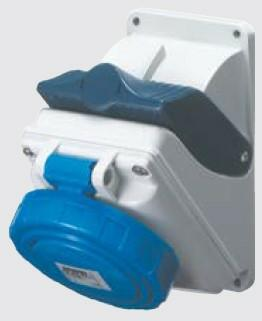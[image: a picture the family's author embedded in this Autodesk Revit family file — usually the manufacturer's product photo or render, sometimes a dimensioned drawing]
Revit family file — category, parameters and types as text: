
# Revit family: Building-ConnessioniIEC309-GEWISS-COMBIBLOC-PRESE-INTERBLOCCATE_IP55_SENZA_FONDO
name_source: partatom
category: Apparecchi elettrici
units: mm (PartAtom-declared; Revit-internal decimal feet)

## family parameters
Condiviso = No
Host = Superficie
Mantenere orientamento annotazione = Sì
Punto di calcolo locali = Sì
Quota connettore circolare = Usa diametro
Taglio con vuoti quando caricato = No
Tipo di parte = Normale

## types (18) — shared parameters
BLOCCO = B=C
Catalogo = BUILDING
Codice Electrocod = 2221
Con fondo = No
FORMULA = 1000 mm  [stored 3.28084 ft]
Frequenza = 50/60 Hz
Glow wire test: = 850 °C (Parti attive) - 650 °C (Parti passive)
Grado di protezione = IP55
IDF = d30aeb64-b42c-4c03-8e60-3032abfc95de
IDT = 73411960965b40fc900c2c175d51bdd6
Immagine tipo = COMBIBLOC55.jpg
L = 155 mm
N.poli = 1
POMELLO = bianco
PRESA = Giallo
Produttore = GEWISS S.p.A.
Prospetto di default = 1219 mm
Protezione = NO (SBF)
Resistenza agli urti = IK08
SEO = Presa interbloccata
STRUTTURA = RAL - 7035
STRUTTURA ALTA = blue
Scheda Tecnica = https://www.gewiss.com
Spostamento_S = 1500 mm
Temperatura di utilizzo = -25 +40 °C
Termopressione con biglia = 125 °C
Tipologia = Compatta
URL = https://www.gewiss.com
VETRO = Vetro
Versione file RFA = 21.4
Voltaggio = 0 V
W = 115 mm

## per-type parameters (varying)
| type | Colore: | Corrente nominale (A) | Descrizione | Modello | N. poli | Riferimento h | Tensione nominale |
| GW66474 - COMBIBLOC S.F.IP55 3P+T 16A 400V 6H | Rosso | 16 | COMBIBLOC S.F.IP55 3P+T 16A 400V 6H | GW66474 | 3P+T | 6 | 380-415V |
| GW66480 - COMBIBLOC S.F.IP55 3P+N+T 32A 110V 4H | Giallo | 32 | COMBIBLOC S.F.IP55 3P+N+T 32A 110V 4H | GW66480 | 3P+N+T | 4 | 100-130V |
| GW66479 - COMBIBLOC S.F.IP55 3P+T 32A 110V 4H | Giallo | 32 | COMBIBLOC S.F.IP55 3P+T 32A 110V 4H | GW66479 | 3P+T | 4 | 100-130V |
| GW66467 - COMBIBLOC S.F.IP55 2P+T 16A 110V 4H | Giallo | 16 | COMBIBLOC S.F.IP55 2P+T 16A 110V 4H | GW66467 | 2P+T | 4 | 100-130V |
| GW66469 - COMBIBLOC S.F.IP55 3P+N+T 16A 110V 4H | Giallo | 16 | COMBIBLOC S.F.IP55 3P+N+T 16A 110V 4H | GW66469 | 3P+N+T | 4 | 100-130V |
| GW66484 - COMBIBLOC S.F.IP55 2P+T 32A 400V 9H | Rosso | 32 | COMBIBLOC S.F.IP55 2P+T 32A 400V 9H | GW66484 | 2P+T | 9 | 380-415V |
| GW66478 - COMBIBLOC S.F.IP55 2P+T 32A 110V 4H | Giallo | 32 | COMBIBLOC S.F.IP55 2P+T 32A 110V 4H | GW66478 | 2P+T | 4 | 100-130V |
| GW66475 - COMBIBLOC S.F.IP55 3P+N+T 16A 400V 6H | Rosso | 16 | COMBIBLOC S.F.IP55 3P+N+T 16A 400V 6H | GW66475 | 3P+N+T | 6 | 380-415V |
| GW66486 - COMBIBLOC S.F.IP55 3P+N+T 32A 400V 6H | Rosso | 32 | COMBIBLOC S.F.IP55 3P+N+T 32A 400V 6H | GW66486 | 3P+N+T | 6 | 380-415V |
| GW66473 - COMBIBLOC S.F.IP55 2P+T 16A 400V 9H | Rosso | 16 | COMBIBLOC S.F.IP55 2P+T 16A 400V 9H | GW66473 | 2P+T | 9 | 380-415V |
| GW66482 - COMBIBLOC S.F.IP55 3P+T 32A 230V 9H | Blu | 32 | COMBIBLOC S.F.IP55 3P+T 32A 230V 9H | GW66482 | 3P+T | 9 | 200-250V |
| GW66483 - COMBIBLOC S.F.IP55 3P+N+T 32A 230V 9H | Blu | 32 | COMBIBLOC S.F.IP55 3P+N+T 32A 230V 9H | GW66483 | 3P+N+T | 9 | 200-250V |
| GW66472 - COMBIBLOC S.F.IP55 3P+N+T 16A 230V 9H | Blu | 16 | COMBIBLOC S.F.IP55 3P+N+T 16A 230V 9H | GW66472 | 3P+N+T | 9 | 200-250V |
| GW66470 - COMBIBLOC S.F.IP55 2P+T 16A 230V 6H | Blu | 16 | COMBIBLOC S.F.IP55 2P+T 16A 230V 6H | GW66470 | 2P+T | 6 | 200-250V |
| GW66485 - COMBIBLOC S.F.IP55 3P+T 32A 400V 6H | Rosso | 32 | COMBIBLOC S.F.IP55 3P+T 32A 400V 6H | GW66485 | 3P+T | 6 | 380-415V |
| GW66481 - COMBIBLOC S.F.IP55 2P+T 32A 230V 6H | Blu | 32 | COMBIBLOC S.F.IP55 2P+T 32A 230V 6H | GW66481 | 2P+T | 6 | 200-250V |
| GW66471 - COMBIBLOC S.F.IP55 3P+T 16A 230V 9H | Blu | 16 | COMBIBLOC S.F.IP55 3P+T 16A 230V 9H | GW66471 | 3P+T | 9 | 200-250V |
| GW66468 - COMBIBLOC S.F.IP55 3P+T 16A 110V 4H | Giallo | 16 | COMBIBLOC S.F.IP55 3P+T 16A 110V 4H | GW66468 | 3P+T | 4 | 100-130V |

note: [stored X ft] marks values corroborated as IEEE doubles in the binary element streams (Revit-internal decimal feet)

## geometry (parser evidence)
native form markers: Sweep x3
no freeform markers — native parametric forms only
